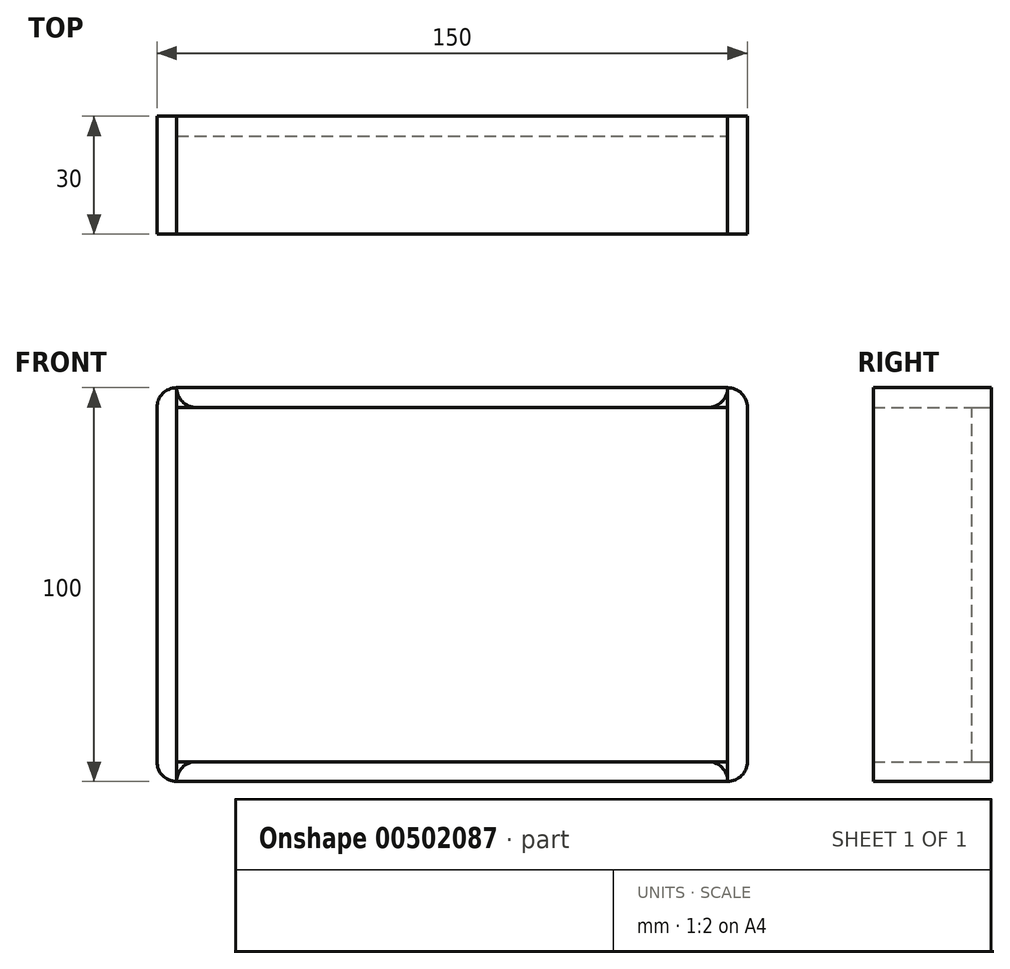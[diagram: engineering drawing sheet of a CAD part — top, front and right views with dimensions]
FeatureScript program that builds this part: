
annotation { "Feature Type Name" : "Feature", "Feature Type Description" : "" }
export const myFeature = defineFeature(function(context is Context, id is Id, definition is map)
    precondition{}
    {
        {
            var Q0;
            Q0=qCreatedBy(makeId("Front.planeOp"),FACE);
            var sketch = newSketch(context, id + "F0", { "sketchPlane" : qUnion([Q0])});
            skLineSegment(sketch, "E0", {"start": v(-75, -50) * mm, "end": v(-75, 50) * mm});
            skLineSegment(sketch, "E1", {"start": v(-75, 50) * mm, "end": v(75, 50) * mm});
            skLineSegment(sketch, "E2", {"start": v(75, 50) * mm, "end": v(75, -50) * mm});
            skLineSegment(sketch, "E3", {"start": v(75, -50) * mm, "end": v(-75, -50) * mm});
            skLineSegment(sketch, "E4", {"start": v(-75, 45) * mm, "end": v(75, 45) * mm});
            skLineSegment(sketch, "E5", {"start": v(-75, -45) * mm, "end": v(75, -45) * mm});
            skLineSegment(sketch, "E6", {"start": v(-70, -50) * mm, "end": v(-70, 50) * mm});
            skLineSegment(sketch, "E7", {"start": v(70, -50) * mm, "end": v(70, 50) * mm});
            skSolve(sketch);
        }
        {
            var Q0;
            {var subQ0=sQuery(id+"F0.wireOp",EDGE,"E6");var subQ1=sQuery(id+"F0.wireOp",EDGE,"E4");var subQ2=makeQuery(id+"F0.imprint","INTERSECT",VERTEX,{"derivedFrom":[subQ1,subQ0]});Q0=makeQuery(id+"F0.imprint","IMPRINT",FACE,{"disambiguationData":[TD([[makeQuery(id+"F0.imprint","IMPRINT",EDGE,{"disambiguationData":[TD([[subQ2,-1.0]])],"derivedFrom":subQ1}),-1.0]])]});}
            extrude(context, id + "F1", {"entities" : qUnion([Q0]), "depth" : 5 * mm});
        }
        {
            var Q0;
            {var subQ0=sQuery(id+"F0.wireOp",EDGE,"E4");var subQ1=sQuery(id+"F0.wireOp",EDGE,"E0");var subQ2=makeQuery(id+"F0.imprint","INTERSECT",VERTEX,{"derivedFrom":[subQ1,subQ0]});Q0=makeQuery(id+"F0.imprint","IMPRINT",FACE,{"disambiguationData":[TD([[makeQuery(id+"F0.imprint","IMPRINT",EDGE,{"disambiguationData":[TD([[subQ2,1.0]])],"derivedFrom":subQ1}),-1.0]])]});}
            var Q1;
            {var subQ0=sQuery(id+"F0.wireOp",EDGE,"E1");var subQ1=sQuery(id+"F0.wireOp",EDGE,"E0");var subQ2=makeQuery(id+"F0.imprint","INTERSECT",VERTEX,{"derivedFrom":[subQ1,subQ0]});Q1=makeQuery(id+"F0.imprint","IMPRINT",FACE,{"disambiguationData":[TD([[makeQuery(id+"F0.imprint","IMPRINT",EDGE,{"disambiguationData":[TD([[subQ2,1.0]])],"derivedFrom":subQ1}),-1.0]])]});}
            var Q2;
            {var subQ0=sQuery(id+"F0.wireOp",EDGE,"E3");var subQ1=sQuery(id+"F0.wireOp",EDGE,"E0");var subQ2=makeQuery(id+"F0.imprint","INTERSECT",VERTEX,{"derivedFrom":[subQ1,subQ0]});Q2=makeQuery(id+"F0.imprint","IMPRINT",FACE,{"disambiguationData":[TD([[makeQuery(id+"F0.imprint","IMPRINT",EDGE,{"disambiguationData":[TD([[subQ2,-1.0]])],"derivedFrom":subQ1}),-1.0]])]});}
            extrude(context, id + "F2", {"entities" : qUnion([Q0, Q1, Q2]), "depth" : 30 * mm});
        }
        {
            var Q0;
            {var subQ0=sQuery(id+"F0.wireOp",EDGE,"E4");var subQ1=sQuery(id+"F0.wireOp",EDGE,"E2");var subQ2=makeQuery(id+"F0.imprint","INTERSECT",VERTEX,{"derivedFrom":[subQ1,subQ0]});Q0=makeQuery(id+"F0.imprint","IMPRINT",FACE,{"disambiguationData":[TD([[makeQuery(id+"F0.imprint","IMPRINT",EDGE,{"disambiguationData":[TD([[subQ2,-1.0]])],"derivedFrom":subQ1}),-1.0]])]});}
            var Q1;
            {var subQ0=sQuery(id+"F0.wireOp",EDGE,"E3");var subQ1=sQuery(id+"F0.wireOp",EDGE,"E2");var subQ2=makeQuery(id+"F0.imprint","INTERSECT",VERTEX,{"derivedFrom":[subQ1,subQ0]});Q1=makeQuery(id+"F0.imprint","IMPRINT",FACE,{"disambiguationData":[TD([[makeQuery(id+"F0.imprint","IMPRINT",EDGE,{"disambiguationData":[TD([[subQ2,1.0]])],"derivedFrom":subQ1}),-1.0]])]});}
            var Q2;
            {var subQ0=sQuery(id+"F0.wireOp",EDGE,"E2");var subQ1=sQuery(id+"F0.wireOp",EDGE,"E1");var subQ2=makeQuery(id+"F0.imprint","INTERSECT",VERTEX,{"derivedFrom":[subQ1,subQ0]});Q2=makeQuery(id+"F0.imprint","IMPRINT",FACE,{"disambiguationData":[TD([[makeQuery(id+"F0.imprint","IMPRINT",EDGE,{"disambiguationData":[TD([[subQ2,1.0]])],"derivedFrom":subQ1}),-1.0]])]});}
            extrude(context, id + "F3", {"entities" : qUnion([Q0, Q1, Q2]), "depth" : 30 * mm});
        }
        {
            var Q0;
            {var subQ0=sQuery(id+"F0.wireOp",EDGE,"E6");var subQ1=sQuery(id+"F0.wireOp",EDGE,"E1");var subQ2=makeQuery(id+"F0.imprint","INTERSECT",VERTEX,{"derivedFrom":[subQ1,subQ0]});Q0=makeQuery(id+"F0.imprint","IMPRINT",FACE,{"disambiguationData":[TD([[makeQuery(id+"F0.imprint","IMPRINT",EDGE,{"disambiguationData":[TD([[subQ2,-1.0]])],"derivedFrom":subQ1}),-1.0]])]});}
            extrude(context, id + "F4", {"entities" : qUnion([Q0]), "depth" : 30 * mm});
        }
        {
            var Q0;
            {var subQ0=sQuery(id+"F0.wireOp",EDGE,"E6");var subQ1=sQuery(id+"F0.wireOp",EDGE,"E3");var subQ2=makeQuery(id+"F0.imprint","INTERSECT",VERTEX,{"derivedFrom":[subQ1,subQ0]});Q0=makeQuery(id+"F0.imprint","IMPRINT",FACE,{"disambiguationData":[TD([[makeQuery(id+"F0.imprint","IMPRINT",EDGE,{"disambiguationData":[TD([[subQ2,1.0]])],"derivedFrom":subQ1}),-1.0]])]});}
            extrude(context, id + "F5", {"entities" : qUnion([Q0]), "depth" : 30 * mm});
        }
        {
            var Q0;
            Q0=makeQuery(id+"F2.opExtrude","SWEPT_EDGE",EDGE,{"disambiguationData":[OSD([sQuery(id+"F0.wireOp",EDGE,"E0"),sQuery(id+"F0.wireOp",EDGE,"E1")])]});
            fillet(context, id + "F6", {"entities" : qUnion([Q0]), "radius" : 5 * mm, "tangentPropagation" : true, "allowEdgeOverflow" : false});
        }
        {
            var Q0;
            Q0=makeQuery(id+"F4.opExtrude","SWEPT_EDGE",EDGE,{"disambiguationData":[OSD([sQuery(id+"F0.wireOp",EDGE,"E4"),sQuery(id+"F0.wireOp",EDGE,"E6")])]});
            fillet(context, id + "F7", {"entities" : qUnion([Q0]), "radius" : 5 * mm, "tangentPropagation" : true, "allowEdgeOverflow" : false});
        }
        {
            var Q0;
            Q0=makeQuery(id+"F2.opExtrude","SWEPT_EDGE",EDGE,{"disambiguationData":[OSD([sQuery(id+"F0.wireOp",EDGE,"E0"),sQuery(id+"F0.wireOp",EDGE,"E3")])]});
            fillet(context, id + "F8", {"entities" : qUnion([Q0]), "radius" : 5 * mm, "tangentPropagation" : true, "allowEdgeOverflow" : false});
        }
        {
            var Q0;
            Q0=makeQuery(id+"F3.opExtrude","SWEPT_EDGE",EDGE,{"disambiguationData":[OSD([sQuery(id+"F0.wireOp",EDGE,"E1"),sQuery(id+"F0.wireOp",EDGE,"E2")])]});
            fillet(context, id + "F9", {"entities" : qUnion([Q0]), "radius" : 5 * mm, "tangentPropagation" : true, "allowEdgeOverflow" : false});
        }
        {
            var Q0;
            Q0=makeQuery(id+"F3.opExtrude","SWEPT_EDGE",EDGE,{"disambiguationData":[OSD([sQuery(id+"F0.wireOp",EDGE,"E2"),sQuery(id+"F0.wireOp",EDGE,"E3")])]});
            fillet(context, id + "F10", {"entities" : qUnion([Q0]), "radius" : 5 * mm, "tangentPropagation" : true, "allowEdgeOverflow" : false});
        }
        {
            var Q0;
            Q0=makeQuery(id+"F5.opExtrude","SWEPT_EDGE",EDGE,{"disambiguationData":[OSD([sQuery(id+"F0.wireOp",EDGE,"E5"),sQuery(id+"F0.wireOp",EDGE,"E6")])]});
            var Q1;
            Q1=makeQuery(id+"F4.opExtrude","SWEPT_EDGE",EDGE,{"disambiguationData":[OSD([sQuery(id+"F0.wireOp",EDGE,"E4"),sQuery(id+"F0.wireOp",EDGE,"E7")])]});
            var Q2;
            Q2=makeQuery(id+"F5.opExtrude","SWEPT_EDGE",EDGE,{"disambiguationData":[OSD([sQuery(id+"F0.wireOp",EDGE,"E5"),sQuery(id+"F0.wireOp",EDGE,"E7")])]});
            fillet(context, id + "F11", {"entities" : qUnion([Q0, Q1, Q2]), "radius" : 5 * mm, "tangentPropagation" : true, "allowEdgeOverflow" : false});
        }
    });
